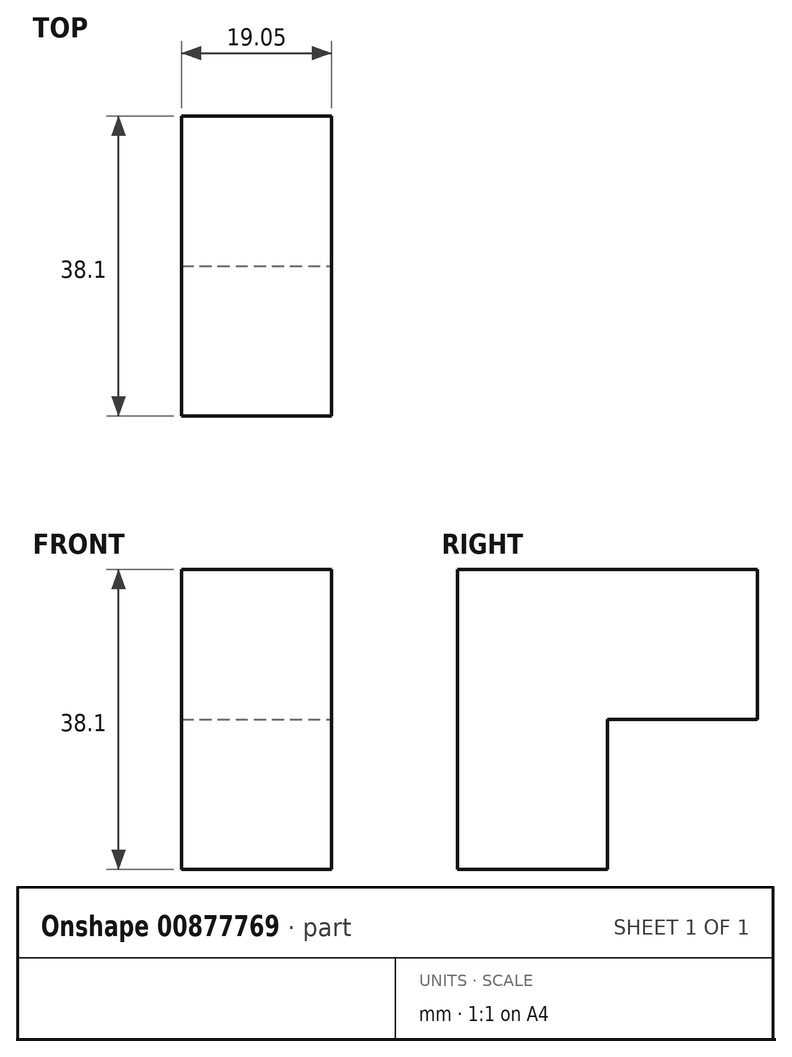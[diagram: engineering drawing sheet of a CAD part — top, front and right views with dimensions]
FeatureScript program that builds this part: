
annotation { "Feature Type Name" : "Feature", "Feature Type Description" : "" }
export const myFeature = defineFeature(function(context is Context, id is Id, definition is map)
    precondition{}
    {
        {
            var Q0;
            Q0=qCreatedBy(makeId("Right.planeOp"),FACE);
            var sketch = newSketch(context, id + "F0", { "sketchPlane" : qUnion([Q0])});
            skLineSegment(sketch, "E0.bottom", {"start": v(0, 0) * mm, "end": v(38.1, 0) * mm});
            skLineSegment(sketch, "E0.top", {"start": v(0, 38.1) * mm, "end": v(38.1, 38.1) * mm});
            skLineSegment(sketch, "E0.left", {"start": v(0, 0) * mm, "end": v(0, 38.1) * mm});
            skLineSegment(sketch, "E0.right", {"start": v(38.1, 0) * mm, "end": v(38.1, 38.1) * mm});
            skSolve(sketch);
        }
        {
            var Q0;
            Q0=qSketchRegion(id+"F0",true);
            extrude(context, id + "F1", {"entities" : qUnion([Q0]), "depth" : 19.05 * mm});
        }
        {
            var Q0;
            Q0=makeQuery(id+"F1.opExtrude","CAP_FACE",FACE,{"disambiguationData":[OSD([sQuery(id+"F0.wireOp",EDGE,"E0.bottom"),sQuery(id+"F0.wireOp",EDGE,"E0.top"),sQuery(id+"F0.wireOp",EDGE,"E0.left"),sQuery(id+"F0.wireOp",EDGE,"E0.right")])],"isStart":false});
            var sketch = newSketch(context, id + "F2", { "sketchPlane" : qUnion([Q0])});
            skLineSegment(sketch, "E1.bottom", {"start": v(38.1, 0) * mm, "end": v(19.05, 0) * mm});
            skLineSegment(sketch, "E1.top", {"start": v(38.1, 19.05) * mm, "end": v(19.05, 19.05) * mm});
            skLineSegment(sketch, "E1.left", {"start": v(38.1, 0) * mm, "end": v(38.1, 19.05) * mm});
            skLineSegment(sketch, "E1.right", {"start": v(19.05, 0) * mm, "end": v(19.05, 19.05) * mm});
            skSolve(sketch);
        }
        {
            var Q0;
            Q0=qSketchRegion(id+"F2",true);
            extrude(context, id + "F3", {"entities" : qUnion([Q0]), "operationType" : NewBodyOperationType.REMOVE, "oppositeDirection" : true, "depth" : 19.05 * mm});
        }
    });
